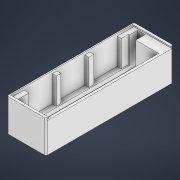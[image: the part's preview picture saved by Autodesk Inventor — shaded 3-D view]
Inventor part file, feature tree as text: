
AUTODESK INVENTOR PART (.ipt)
format: ipt  version: 2022 (Build 260153000, 153)  size: 349,696 bytes
history: native  units: mm
features: extrude x13, sketch x13, chamfer x2, projected_geometry x1
ambient origin geometry x8: Origin, YZ Plane, XZ Plane, XY Plane, X Axis, Y Axis, Z Axis, Center Point
bodies: 实体1 (feature_tree)
feature tree (29):
  extrude  "拉伸1"  Depth=94.0mm
  extrude  "拉伸2"  Depth=1.8mm
  extrude  "拉伸3"  Depth=1.8mm
  extrude  "拉伸4"  Depth=24.2mm TaperAngle=0.0deg
  extrude  "拉伸5"  Depth=31.0mm
  extrude  "拉伸6"  Depth=55.0mm
  extrude  "拉伸7"  Depth=79.0mm
  extrude  "拉伸8"  Depth=3.0mm TaperAngle=0.0deg
  extrude  "拉伸9"  Depth=51.5mm
  extrude  "拉伸10"  Depth=10.5mm
  extrude  "拉伸11"  Depth=3.0mm TaperAngle=0.0deg
  extrude  "拉伸12"  Depth=4.8mm
  extrude  "拉伸13"  Depth=9.0mm
  chamfer  "倒角1"  Distance=0.5mm
  chamfer  "倒角2"  Distance=3.0mm
  sketch  "草图1"  dims[d4=26.0mm d5=94.0mm]
  sketch  "草图2"  dims[d6=30.0mm d7=0.0mm d8=1.8mm]
  sketch  "草图3"  dims[d9=1.8mm d10=1.8mm]
  sketch  "草图4"  dims[d11=1.8mm d12=24.2mm d13=0.0mm]
  sketch  "草图5"  dims[d14=10.0mm d15=31.0mm]
  sketch  "草图6"  dims[d16=34.4mm d17=55.0mm]
  sketch  "草图7"  dims[d18=58.8mm d19=79.0mm]
  sketch  "草图8"  dims[d20=3.0mm d21=3.0mm d22=0.0mm]
  sketch  "草图9"  dims[d23=5.5mm d24=51.5mm]
  sketch  "草图10"  dims[d25=3.2mm d26=10.5mm]
  sketch  "草图11"  dims[d27=1.0mm d28=3.0mm d29=0.0mm]
  sketch  "草图12"  dims[d30=1.6mm d31=4.8mm]
  projected_geometry  "投影回路1"
  sketch  "草图13"  dims[d32=2.6mm d33=9.0mm d34=0.5mm d35=0.0mm d36=3.0mm d37=1.5mm d38=10.5mm d39=13.3mm d40=19.6mm d41=22.4mm d42=28.5mm d43=31.5mm d44=37.5mm d45=40.6mm d46=3.0mm d47=0.0mm d48=1.0mm d49=0.0mm d50=1.0mm d51=0.0mm d52=10.0mm d53=6.0mm d54=0.75mm d55=0.0mm d56=0.75mm d57=0.0mm d58=9.0mm d59=9.0mm d60=4.0mm d61=10.0mm d62=0.0mm d63=17.0mm d64=7.0mm d65=0.0mm d66=1.8mm d69=1.8mm d70=0.0mm d71=1.0mm d72=2.0mm d73=45.0deg d74=0.5mm d75=2.0mm d76=45.0deg]
